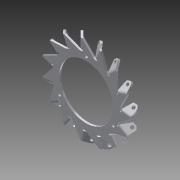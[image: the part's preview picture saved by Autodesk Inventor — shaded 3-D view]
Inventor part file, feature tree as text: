
AUTODESK INVENTOR PART (.ipt)
format: ipt  version: 2015 SP1 (Build 190203100, 203)  size: 518,144 bytes
history: native  units: in
note: dims shown in document units (in); Inventor stores cm internally (conversion verified against a paired STEP export)
features: fillet x1, other x1, imported_body x1
ambient origin geometry x8: Origin, YZ Plane, XZ Plane, XY Plane, X Axis, Y Axis, Z Axis, Center Point
bodies: Body1 (feature_tree)
feature tree (3):
  fillet  "Fillet1"  [1 undecoded]
  other  "Left plate HD.ipt1"
  imported_body  "Base1"
note: 1 required parameter value undecoded (feature->parameter linkage not recoverable at this tier; creation-order binding heuristic only, values carry confidence <= 0.55)
